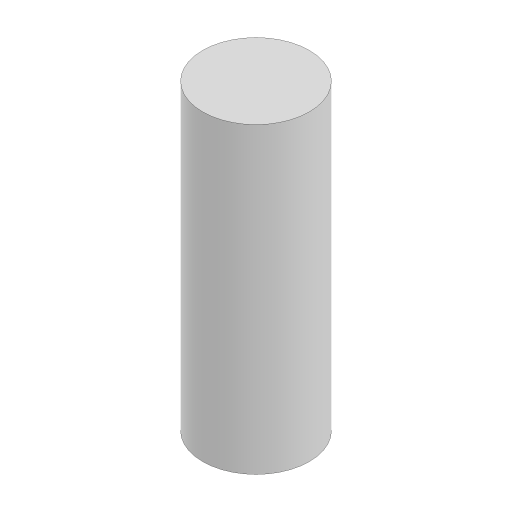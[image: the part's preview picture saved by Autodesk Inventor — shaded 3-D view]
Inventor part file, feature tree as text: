
AUTODESK INVENTOR PART (.ipt)
format: ipt  version: 2024.2 (Build 282272000, 272)  size: 77,824 bytes
history: native  units: in
note: dims shown in document units (in); Inventor stores cm internally (conversion verified against a paired STEP export)
features: extrude x1, sketch x1
ambient origin geometry x8: Origin, YZ Plane, XZ Plane, XY Plane, X Axis, Y Axis, Z Axis, Center Point
bodies: Solid1 (feature_tree)
feature tree (2):
  extrude  "Extrusion1"  Depth=0.625in TaperAngle=0.0deg
  sketch  "Sketch1"  dims[d0=0.22in d1=0.625in d2=0.0in]
